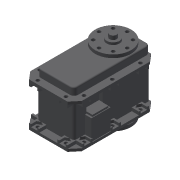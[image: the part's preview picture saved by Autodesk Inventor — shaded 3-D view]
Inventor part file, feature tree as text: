
AUTODESK INVENTOR PART (.ipt)
format: ipt  version: 2020.5 (Build 245400000, 400)  size: 748,544 bytes
history: native  units: mm (DEFAULTED — no unit token found)
features: other x5, sketch x4, extrude x2, projected_geometry x2, reference x1
ambient origin geometry x8: Origin, YZ Plane, XZ Plane, XY Plane, X Axis, Y Axis, Z Axis, Center Point
bodies: Body1 (feature_tree)
feature tree (14):
  other  "솔리드1"
  other  "기준1"
  extrude  "돌출1"  Depth=3.0mm TaperAngle=0.0deg
  sketch  "스케치2"
  extrude  "돌출2"  Depth=3.0mm TaperAngle=0.0deg
  sketch  "스케치4"
  sketch  "스케치1"
  reference  "참조1"
  sketch  "스케치3"
  projected_geometry  "투영된 루프1"
  projected_geometry  "투영된 루프2"
  parser-record x1  (decoder bookkeeping rows leaked as tree rows — omitted from the tree; the rows remain in map.json)
  other  "휴머노이드설계.iam"
  other  "EX106_N:5"
note: 1 file-system path scrubbed to <path> (originals preserved in map.json)
